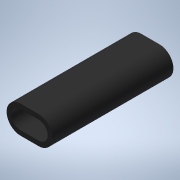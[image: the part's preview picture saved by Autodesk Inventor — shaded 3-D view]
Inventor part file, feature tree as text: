
AUTODESK INVENTOR PART (.ipt)
format: ipt  version: 2020 (Build 240168000, 168)  size: 1,340,928 bytes
history: native  units: mm
features: sketch x3, emboss x2, projected_geometry x2, extrude x1
ambient origin geometry x8: Origin, YZ Plane, XZ Plane, XY Plane, X Axis, Y Axis, Z Axis, Center Point
bodies: Solid1 (feature_tree)
feature tree (8):
  extrude  "Extrusion1"  Depth=30.0mm
  emboss  "Emboss1"
  emboss  "Emboss2"
  sketch  "Sketch1"  dims[d0=15.0mm d1=30.0mm]
  sketch  "Sketch3"  dims[d2=8.0mm]
  projected_geometry  "Projected Loop1"
  sketch  "Sketch4"  dims[d3=200.0mm d4=0.0mm d5=1.0mm d6=0.0mm d7=1.0mm d8=0.0mm]
  projected_geometry  "Projected Loop2"
